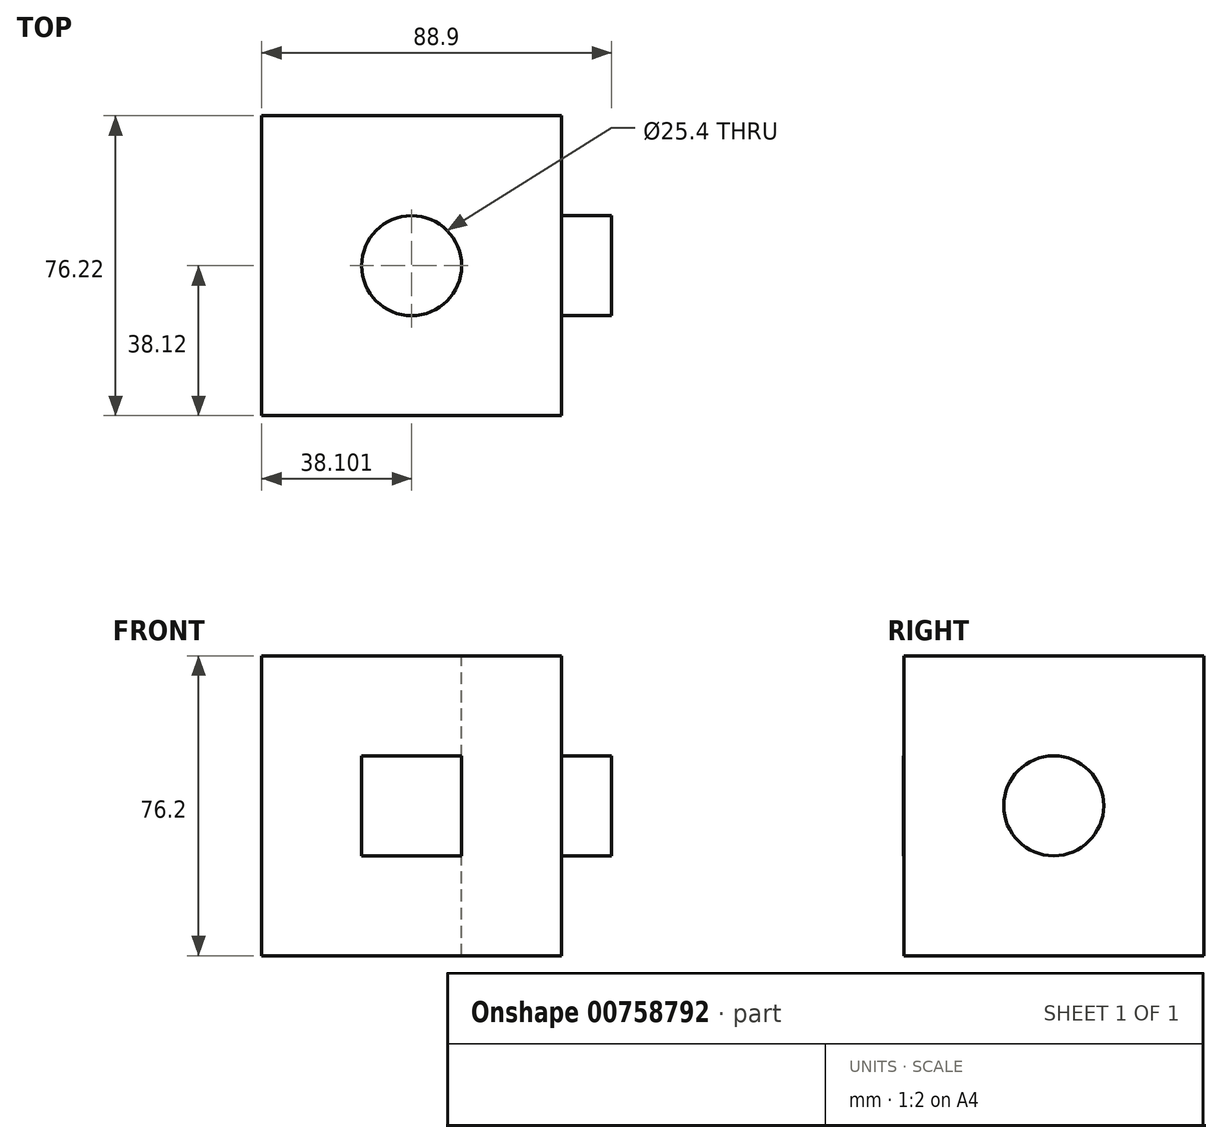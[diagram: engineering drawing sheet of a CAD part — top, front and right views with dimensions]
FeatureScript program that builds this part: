
annotation { "Feature Type Name" : "Feature", "Feature Type Description" : "" }
export const myFeature = defineFeature(function(context is Context, id is Id, definition is map)
    precondition{}
    {
        {
            var Q0;
            Q0=qCreatedBy(makeId("Front.planeOp"),FACE);
            var sketch = newSketch(context, id + "F0", { "sketchPlane" : qUnion([Q0])});
            skLineSegment(sketch, "E0.bottom", {"start": v(-46.42, 48.96) * mm, "end": v(29.78, 48.96) * mm});
            skLineSegment(sketch, "E0.top", {"start": v(-46.42, -27.24) * mm, "end": v(29.78, -27.24) * mm});
            skLineSegment(sketch, "E0.left", {"start": v(-46.42, 48.96) * mm, "end": v(-46.42, -27.24) * mm});
            skLineSegment(sketch, "E0.right", {"start": v(29.78, 48.96) * mm, "end": v(29.78, -27.24) * mm});
            skSolve(sketch);
        }
        {
            var Q0;
            Q0=makeQuery(id+"F0.imprint","IMPRINT",FACE,{"disambiguationData":[TD([[makeQuery(id+"F0.imprint","IMPRINT",EDGE,{"derivedFrom":sQuery(id+"F0.wireOp",EDGE,"E0.bottom")}),-1.0]])]});
            extrude(context, id + "F1", {"entities" : qUnion([Q0]), "depth" : 76.2 * mm, "offsetDistance" : 25.4 * mm});
        }
        {
            var Q0;
            Q0=makeQuery(id+"F1.opExtrude","CAP_FACE",FACE,{"disambiguationData":[OSD([sQuery(id+"F0.wireOp",EDGE,"E0.bottom"),sQuery(id+"F0.wireOp",EDGE,"E0.top"),sQuery(id+"F0.wireOp",EDGE,"E0.left"),sQuery(id+"F0.wireOp",EDGE,"E0.right")])],"isStart":false});
            var sketch = newSketch(context, id + "F2", { "sketchPlane" : qUnion([Q0])});
            skLineSegment(sketch, "E1.bottom", {"start": v(-21.02, 23.56) * mm, "end": v(4.38, 23.56) * mm});
            skLineSegment(sketch, "E1.top", {"start": v(-21.02, -1.84) * mm, "end": v(4.38, -1.84) * mm});
            skLineSegment(sketch, "E1.left", {"start": v(-21.02, 23.56) * mm, "end": v(-21.02, -1.84) * mm});
            skLineSegment(sketch, "E1.right", {"start": v(4.38, 23.56) * mm, "end": v(4.38, -1.84) * mm});
            skSolve(sketch);
        }
        {
            var Q0;
            Q0=makeQuery(id+"F2.imprint","IMPRINT",FACE,{"disambiguationData":[TD([[makeQuery(id+"F2.imprint","IMPRINT",EDGE,{"derivedFrom":sQuery(id+"F2.wireOp",EDGE,"E1.bottom")}),-1.0]])]});
            extrude(context, id + "F3", {"entities" : qUnion([Q0]), "operationType" : NewBodyOperationType.ADD, "depth" : 1 / 50.8 * mm, "offsetDistance" : 25.4 * mm});
        }
        {
            var Q0;
            Q0=makeQuery(id+"F1.opExtrude","SWEPT_FACE",FACE,{"disambiguationData":[OSD([sQuery(id+"F0.wireOp",EDGE,"E0.right")])]});
            var sketch = newSketch(context, id + "F4", { "sketchPlane" : qUnion([Q0])});
            skCircle(sketch, "E2", {"center": v(-38.1, 10.86) * mm, "radius": 12.7 * mm});
            skSolve(sketch);
        }
        {
            var Q0;
            Q0=makeQuery(id+"F4.imprint","IMPRINT",FACE,{"disambiguationData":[TD([[makeQuery(id+"F4.imprint","IMPRINT",EDGE,{"derivedFrom":sQuery(id+"F4.wireOp",EDGE,"E2")}),1.0]])]});
            extrude(context, id + "F5", {"entities" : qUnion([Q0]), "operationType" : NewBodyOperationType.ADD, "depth" : 12.7 * mm, "offsetDistance" : 25.4 * mm});
        }
        {
            var Q0;
            Q0=makeQuery(id+"F1.opExtrude","SWEPT_FACE",FACE,{"disambiguationData":[OSD([sQuery(id+"F0.wireOp",EDGE,"E0.bottom")])]});
            var sketch = newSketch(context, id + "F6", { "sketchPlane" : qUnion([Q0])});
            skPoint(sketch, "E3", {"position": v(-8.32, -38.1) * mm});
            skSolve(sketch);
        }
        {
            var Q0;
            Q0=sQuery(id+"F6.wireOp",VERTEX,"E3");
            var Q1;
            Q1=makeQuery(id+"F1.opExtrude","SWEPT_BODY",BODY,{"disambiguationData":[OSD([sQuery(id+"F0.wireOp",EDGE,"E0.bottom"),sQuery(id+"F0.wireOp",EDGE,"E0.top"),sQuery(id+"F0.wireOp",EDGE,"E0.left"),sQuery(id+"F0.wireOp",EDGE,"E0.right")])]});
            hole(context, id + "F7", {"style" : HoleStyle.SIMPLE, "endStyle" : HoleEndStyle.THROUGH, "holeDiameter" : 25.4 * mm, "majorDiameter" : 6.35 * mm, "isTappedThrough" : true, "tappedDepth" : 12.7 * mm, "tapClearance" : 3, "locations" : qUnion([Q0]), "scope" : qUnion([Q1])});
        }
    });
